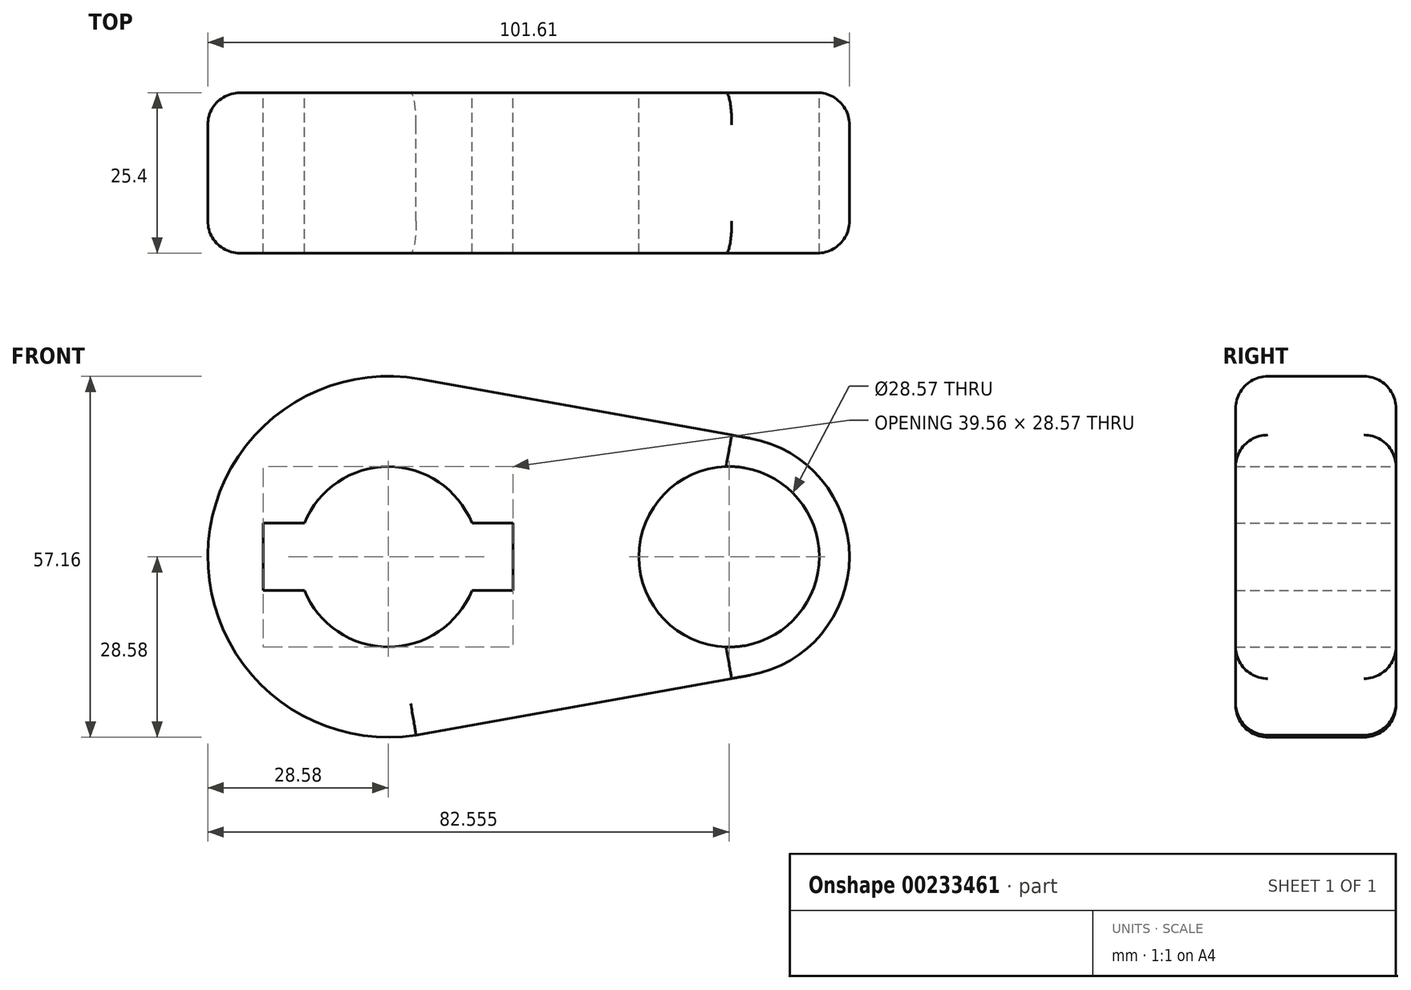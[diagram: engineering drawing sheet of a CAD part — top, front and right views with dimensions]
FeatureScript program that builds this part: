
annotation { "Feature Type Name" : "Feature", "Feature Type Description" : "" }
export const myFeature = defineFeature(function(context is Context, id is Id, definition is map)
    precondition{}
    {
        {
            var Q0;
            Q0=qCreatedBy(makeId("Front.planeOp"),FACE);
            var sketch = newSketch(context, id + "F0", { "sketchPlane" : qUnion([Q0])});
            skCircle(sketch, "E0", {"center": v(0, 0) * mm, "radius": 28.58 * mm});
            skCircle(sketch, "E1", {"center": v(53.98, 0) * mm, "radius": 19.05 * mm});
            skLineSegment(sketch, "E2", {"start": v(5.04, 28.13) * mm, "end": v(57.34, 18.75) * mm});
            skLineSegment(sketch, "E3", {"start": v(4.4, -28.23) * mm, "end": v(57.33, -18.75) * mm});
            skCircle(sketch, "E4", {"center": v(53.98, 0) * mm, "radius": 14.29 * mm});
            skCircle(sketch, "E5", {"center": v(0, 0) * mm, "radius": 14.29 * mm});
            skLineSegment(sketch, "E6.bottom", {"start": v(-19.78, 5.33) * mm, "end": v(19.78, 5.33) * mm});
            skLineSegment(sketch, "E6.top", {"start": v(-19.78, -5.33) * mm, "end": v(19.78, -5.33) * mm});
            skLineSegment(sketch, "E6.left", {"start": v(-19.78, 5.33) * mm, "end": v(-19.78, -5.33) * mm});
            skLineSegment(sketch, "E6.right", {"start": v(19.78, 5.33) * mm, "end": v(19.78, -5.33) * mm});
            skSolve(sketch);
        }
        {
            var Q0;
            Q0=makeQuery(id+"F0.imprint","IMPRINT",FACE,{"disambiguationData":[TD([[makeQuery(id+"F0.imprint","IMPRINT",EDGE,{"derivedFrom":sQuery(id+"F0.wireOp",EDGE,"E4")}),-1.0]])]});
            var Q1;
            {var subQ0=sQuery(id+"F0.wireOp",EDGE,"E2");Q1=makeQuery(id+"F0.imprint","IMPRINT",FACE,{"disambiguationData":[TD([[makeQuery(id+"F0.imprint","IMPRINT",EDGE,{"derivedFrom":subQ0}),-1.0]])]});}
            var Q2;
            {var subQ0=sQuery(id+"F0.wireOp",EDGE,"E6.left");Q2=makeQuery(id+"F0.imprint","IMPRINT",FACE,{"disambiguationData":[TD([[makeQuery(id+"F0.imprint","IMPRINT",EDGE,{"derivedFrom":subQ0}),-1.0]])]});}
            extrude(context, id + "F1", {"entities" : qUnion([Q0, Q1, Q2]), "depth" : 25.4 * mm});
        }
        {
            var Q0;
            Q0=makeQuery(id+"F1.opExtrude","CAP_EDGE",EDGE,{"disambiguationData":[OSD([sQuery(id+"F0.wireOp",EDGE,"E2")])],"isStart":false});
            var Q1;
            Q1=makeQuery(id+"F1.opExtrude","CAP_EDGE",EDGE,{"disambiguationData":[OSD([sQuery(id+"F0.wireOp",EDGE,"E0")])],"isStart":false});
            var Q2;
            Q2=makeQuery(id+"F1.opExtrude","CAP_EDGE",EDGE,{"disambiguationData":[OSD([sQuery(id+"F0.wireOp",EDGE,"E3")])],"isStart":false});
            var Q3;
            Q3=makeQuery(id+"F1.opExtrude","CAP_EDGE",EDGE,{"disambiguationData":[OSD([sQuery(id+"F0.wireOp",EDGE,"E1")])],"isStart":false});
            fillet(context, id + "F2", {"entities" : qUnion([Q0, Q1, Q2, Q3]), "radius" : 5.08 * mm, "tangentPropagation" : true, "allowEdgeOverflow" : false});
        }
        {
            var Q0;
            Q0=makeQuery(id+"F1.opExtrude","CAP_EDGE",EDGE,{"disambiguationData":[OSD([sQuery(id+"F0.wireOp",EDGE,"E3")])],"isStart":true});
            var Q1;
            Q1=makeQuery(id+"F1.opExtrude","CAP_EDGE",EDGE,{"disambiguationData":[OSD([sQuery(id+"F0.wireOp",EDGE,"E0")])],"isStart":true});
            var Q2;
            Q2=makeQuery(id+"F1.opExtrude","CAP_EDGE",EDGE,{"disambiguationData":[OSD([sQuery(id+"F0.wireOp",EDGE,"E2")])],"isStart":true});
            var Q3;
            Q3=makeQuery(id+"F1.opExtrude","CAP_EDGE",EDGE,{"disambiguationData":[OSD([sQuery(id+"F0.wireOp",EDGE,"E1")])],"isStart":true});
            fillet(context, id + "F3", {"entities" : qUnion([Q0, Q1, Q2, Q3]), "radius" : 5.08 * mm, "tangentPropagation" : true, "allowEdgeOverflow" : false});
        }
    });
